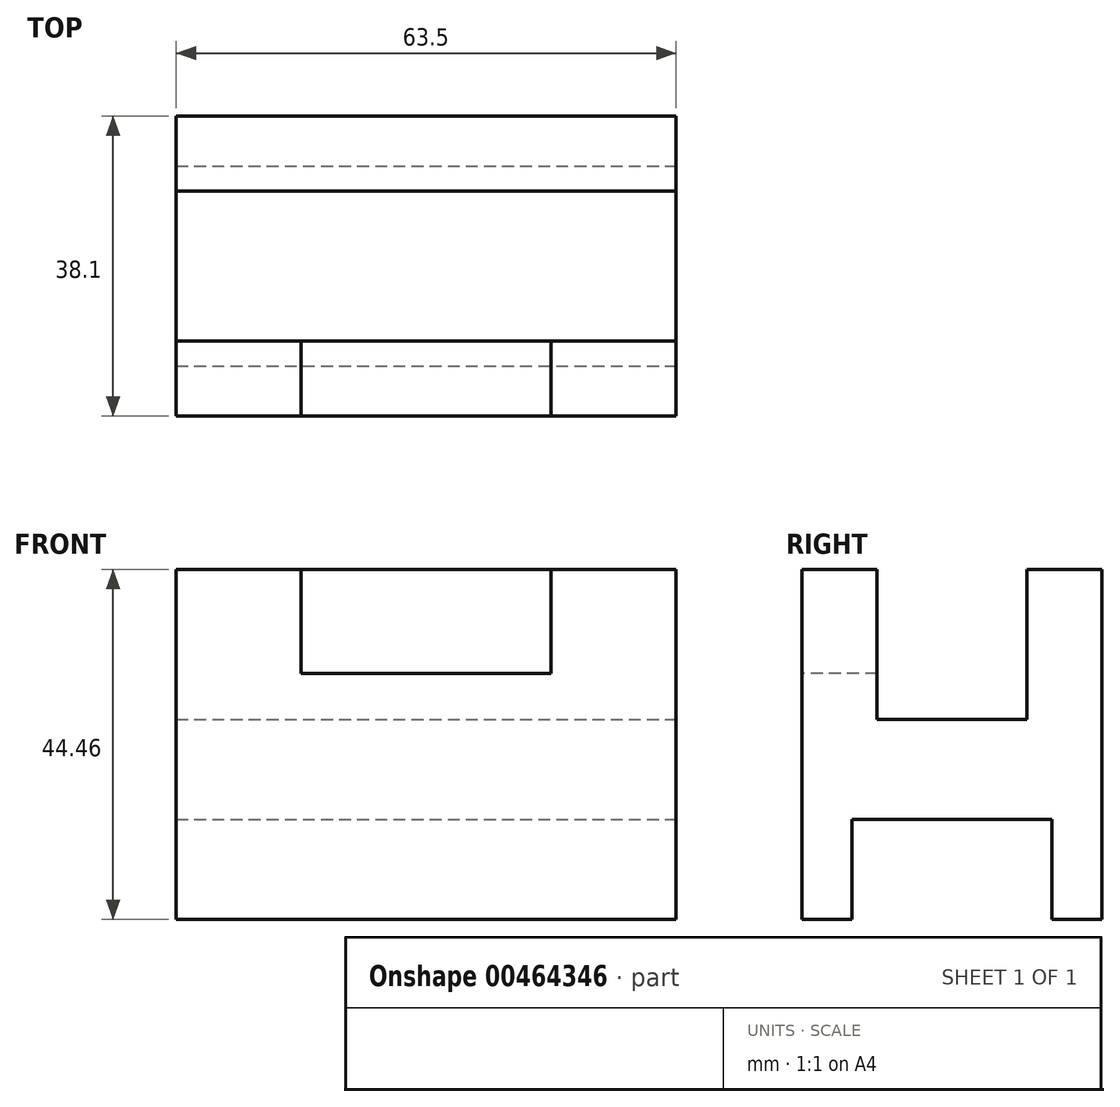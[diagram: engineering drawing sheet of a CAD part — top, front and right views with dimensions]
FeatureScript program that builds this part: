
annotation { "Feature Type Name" : "Feature", "Feature Type Description" : "" }
export const myFeature = defineFeature(function(context is Context, id is Id, definition is map)
    precondition{}
    {
        {
            var Q0;
            Q0=qCreatedBy(makeId("Front.planeOp"),FACE);
            var sketch = newSketch(context, id + "F0", { "sketchPlane" : qUnion([Q0])});
            skLineSegment(sketch, "E0.bottom", {"start": v(-31.75, 22.23) * mm, "end": v(31.75, 22.23) * mm});
            skLineSegment(sketch, "E0.top", {"start": v(-31.75, -22.22) * mm, "end": v(31.75, -22.22) * mm});
            skLineSegment(sketch, "E0.left", {"start": v(-31.75, 22.23) * mm, "end": v(-31.75, -22.22) * mm});
            skLineSegment(sketch, "E0.right", {"start": v(31.75, 22.22) * mm, "end": v(31.75, -22.23) * mm});
            skPoint(sketch, "E0.middle", {"position": v(0, 0) * mm});
            skSolve(sketch);
        }
        {
            var Q0;
            Q0 = qSketchRegion(id + "F0", true);
            extrude(context, id + "F1", {"entities" : qUnion([Q0]), "depth" : 38.1 * mm});
        }
        {
            var Q0;
            Q0=makeQuery(id+"F1.opExtrude","CAP_FACE",FACE,{"disambiguationData":[OSD([sQuery(id+"F0.wireOp",EDGE,"E0.bottom"),sQuery(id+"F0.wireOp",EDGE,"E0.top"),sQuery(id+"F0.wireOp",EDGE,"E0.left"),sQuery(id+"F0.wireOp",EDGE,"E0.right")])],"isStart":false});
            var sketch = newSketch(context, id + "F2", { "sketchPlane" : qUnion([Q0])});
            skLineSegment(sketch, "E1.bottom", {"start": v(-15.87, 22.23) * mm, "end": v(15.87, 22.23) * mm});
            skLineSegment(sketch, "E1.top", {"start": v(-15.88, 9.04) * mm, "end": v(15.88, 9.04) * mm});
            skLineSegment(sketch, "E1.left", {"start": v(-15.88, 22.23) * mm, "end": v(-15.88, 9.04) * mm});
            skLineSegment(sketch, "E1.right", {"start": v(15.88, 22.23) * mm, "end": v(15.88, 9.04) * mm});
            skSolve(sketch);
        }
        {
            var Q0;
            Q0 = qSketchRegion(id + "F2", true);
            extrude(context, id + "F3", {"entities" : qUnion([Q0]), "operationType" : NewBodyOperationType.REMOVE, "oppositeDirection" : true, "depth" : 9.52 * mm});
        }
        {
            var Q0;
            Q0=makeQuery(id+"F1.opExtrude","SWEPT_FACE",FACE,{"disambiguationData":[OSD([sQuery(id+"F0.wireOp",EDGE,"E0.bottom")])]});
            var sketch = newSketch(context, id + "F4", { "sketchPlane" : qUnion([Q0])});
            skLineSegment(sketch, "E2.bottom", {"start": v(-31.75, -9.53) * mm, "end": v(31.75, -9.53) * mm});
            skLineSegment(sketch, "E2.top", {"start": v(-31.75, -28.58) * mm, "end": v(31.75, -28.58) * mm});
            skLineSegment(sketch, "E2.left", {"start": v(-31.75, -9.53) * mm, "end": v(-31.75, -28.58) * mm});
            skLineSegment(sketch, "E2.right", {"start": v(31.75, -9.53) * mm, "end": v(31.75, -28.58) * mm});
            skSolve(sketch);
        }
        {
            var Q0;
            Q0 = qSketchRegion(id + "F4", true);
            extrude(context, id + "F5", {"entities" : qUnion([Q0]), "operationType" : NewBodyOperationType.REMOVE, "oppositeDirection" : true, "depth" : 19.05 * mm});
        }
        {
            var Q0;
            Q0=makeQuery(id+"F1.opExtrude","SWEPT_FACE",FACE,{"disambiguationData":[OSD([sQuery(id+"F0.wireOp",EDGE,"E0.right")])]});
            var sketch = newSketch(context, id + "F6", { "sketchPlane" : qUnion([Q0])});
            skLineSegment(sketch, "E3.bottom", {"start": v(-31.75, -22.22) * mm, "end": v(-6.35, -22.22) * mm});
            skLineSegment(sketch, "E3.top", {"start": v(-31.75, -9.52) * mm, "end": v(-6.35, -9.52) * mm});
            skLineSegment(sketch, "E3.left", {"start": v(-31.75, -22.22) * mm, "end": v(-31.75, -9.52) * mm});
            skLineSegment(sketch, "E3.right", {"start": v(-6.35, -22.22) * mm, "end": v(-6.35, -9.52) * mm});
            skSolve(sketch);
        }
        {
            var Q0;
            Q0 = qSketchRegion(id + "F6", true);
            extrude(context, id + "F7", {"entities" : qUnion([Q0]), "operationType" : NewBodyOperationType.REMOVE, "endBound" : BoundingType.THROUGH_ALL, "oppositeDirection" : true, "depth" : 25.4 * mm});
        }
    });
